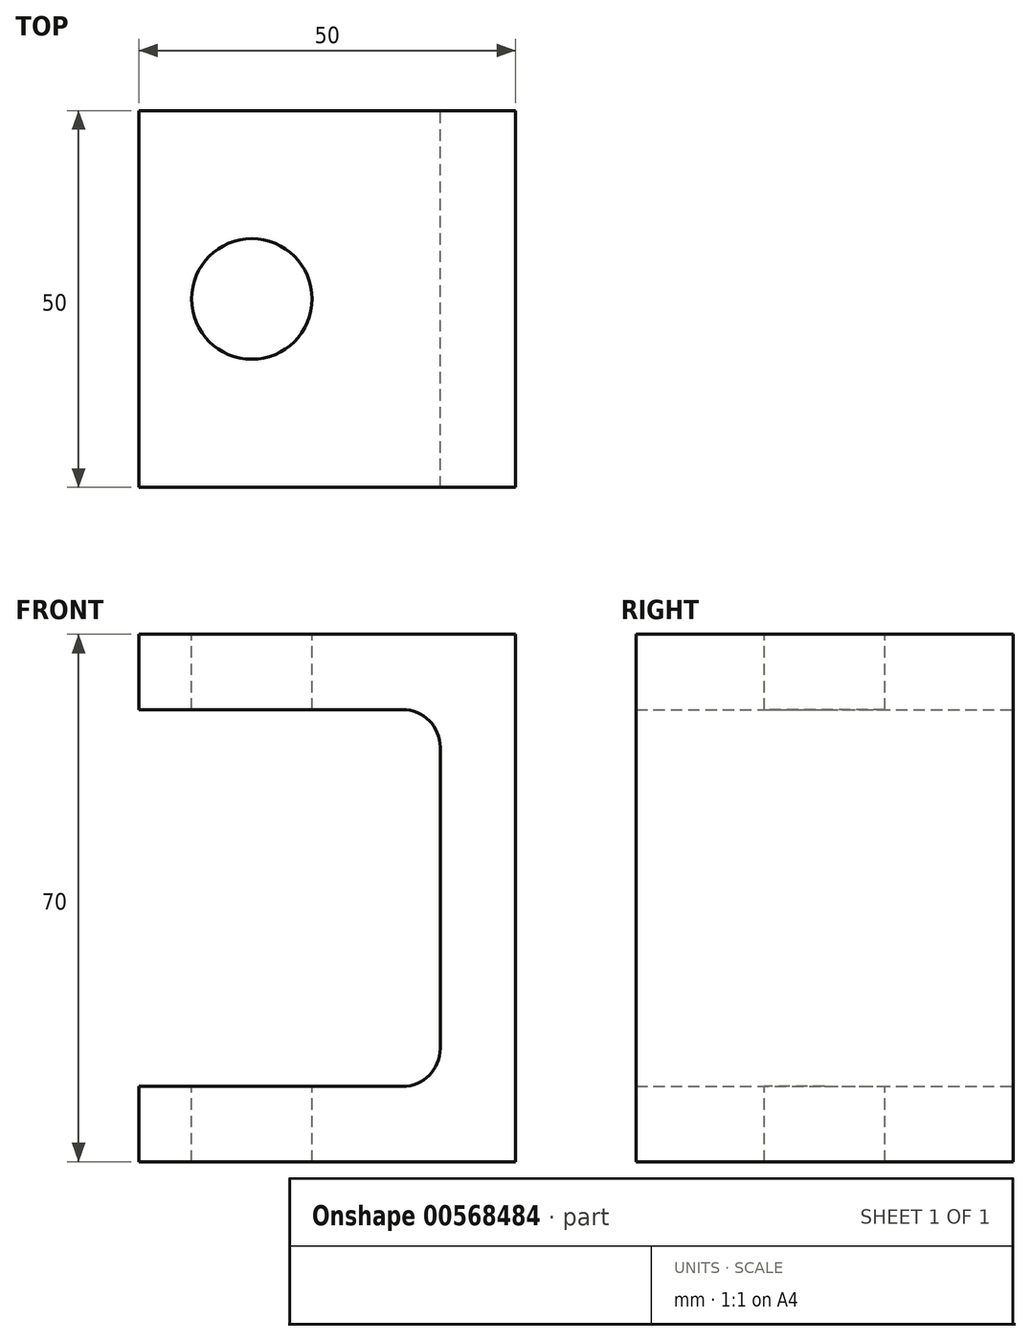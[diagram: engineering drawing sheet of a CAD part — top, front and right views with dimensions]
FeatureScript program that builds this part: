
annotation { "Feature Type Name" : "Feature", "Feature Type Description" : "" }
export const myFeature = defineFeature(function(context is Context, id is Id, definition is map)
    precondition{}
    {
        {
            var Q0;
            Q0=qCreatedBy(makeId("Front.planeOp"),FACE);
            var sketch = newSketch(context, id + "F0", { "sketchPlane" : qUnion([Q0])});
            skLineSegment(sketch, "E0", {"start": v(50, 0) * mm, "end": v(50, 35) * mm});
            skLineSegment(sketch, "E1", {"start": v(50, 35) * mm, "end": v(0, 35) * mm});
            skLineSegment(sketch, "E2", {"start": v(0, 35) * mm, "end": v(0, 25) * mm});
            skLineSegment(sketch, "E3", {"start": v(0, 25) * mm, "end": v(40, 25) * mm});
            skLineSegment(sketch, "E4", {"start": v(40, 25) * mm, "end": v(40, 0) * mm});
            skLineSegment(sketch, "E5", {"start": v(0, 0) * mm, "end": v(0, 66.42) * mm, "construction": true});
            skLineSegment(sketch, "E6", {"start": v(40, 0) * mm, "end": v(50, 0) * mm});
            skSolve(sketch);
        }
        {
            var Q0;
            Q0=makeQuery(id+"F0.imprint","IMPRINT",FACE,{"disambiguationData":[TD([[makeQuery(id+"F0.imprint","IMPRINT",EDGE,{"derivedFrom":sQuery(id+"F0.wireOp",EDGE,"E0")}),1.0]])]});
            extrude(context, id + "F1", {"entities" : qUnion([Q0]), "endBound" : BoundingType.SYMMETRIC, "depth" : 50 * mm, "offsetDistance" : 25 * mm});
        }
        {
            var Q0;
            Q0=makeQuery(id+"F1.opExtrude","SWEPT_BODY",BODY,{"disambiguationData":[OSD([sQuery(id+"F0.wireOp",EDGE,"E0"),sQuery(id+"F0.wireOp",EDGE,"E1"),sQuery(id+"F0.wireOp",EDGE,"E2"),sQuery(id+"F0.wireOp",EDGE,"E3"),sQuery(id+"F0.wireOp",EDGE,"E4"),sQuery(id+"F0.wireOp",EDGE,"E6")])]});
            var Q1;
            Q1=qCreatedBy(makeId("Top.planeOp"),FACE);
            mirror(context, id + "F2", {"operationType" : NewBodyOperationType.ADD, "entities" : qUnion([Q0]), "mirrorPlane" : qUnion([Q1])});
        }
        {
            var Q0;
            Q0=makeQuery(id+"F1.opExtrude","SWEPT_FACE",FACE,{"disambiguationData":[OSD([sQuery(id+"F0.wireOp",EDGE,"E1")])]});
            var sketch = newSketch(context, id + "F3", { "sketchPlane" : qUnion([Q0])});
            skPoint(sketch, "E7", {"position": v(15, 0) * mm});
            skPoint(sketch, "E8.0", {"position": v(40, 25) * mm});
            skLineSegment(sketch, "E9", {"start": v(40, 25) * mm, "end": v(40, -25) * mm, "construction": true});
            skSolve(sketch);
        }
        {
            var Q0;
            Q0=sQuery(id+"F3.wireOp",VERTEX,"E7");
            var Q1;
            Q1=makeQuery(id+"F1.opExtrude","SWEPT_BODY",BODY,{"disambiguationData":[OSD([sQuery(id+"F0.wireOp",EDGE,"E0"),sQuery(id+"F0.wireOp",EDGE,"E1"),sQuery(id+"F0.wireOp",EDGE,"E2"),sQuery(id+"F0.wireOp",EDGE,"E3"),sQuery(id+"F0.wireOp",EDGE,"E4"),sQuery(id+"F0.wireOp",EDGE,"E6")])]});
            hole(context, id + "F4", {"style" : HoleStyle.SIMPLE, "endStyle" : HoleEndStyle.THROUGH, "holeDiameter" : 16 * mm, "isTappedThrough" : true, "tappedDepth" : 12 * mm, "tapClearance" : 3, "locations" : qUnion([Q0]), "scope" : qUnion([Q1])});
        }
        {
            var Q0;
            Q0=makeQuery(id+"F1.opExtrude","SWEPT_EDGE",EDGE,{"disambiguationData":[OSD([sQuery(id+"F0.wireOp",EDGE,"E3"),sQuery(id+"F0.wireOp",EDGE,"E4")])]});
            var Q1;
            Q1=makeQuery(id+"F2.opPattern","COPY",EDGE,{"derivedFrom":makeQuery(id+"F1.opExtrude","SWEPT_EDGE",EDGE,{"disambiguationData":[OSD([sQuery(id+"F0.wireOp",EDGE,"E3"),sQuery(id+"F0.wireOp",EDGE,"E4")])]}),"instanceName":"1"});
            fillet(context, id + "F5", {"entities" : qUnion([Q0, Q1]), "radius" : 5 * mm, "tangentPropagation" : true, "allowEdgeOverflow" : false});
        }
    });
